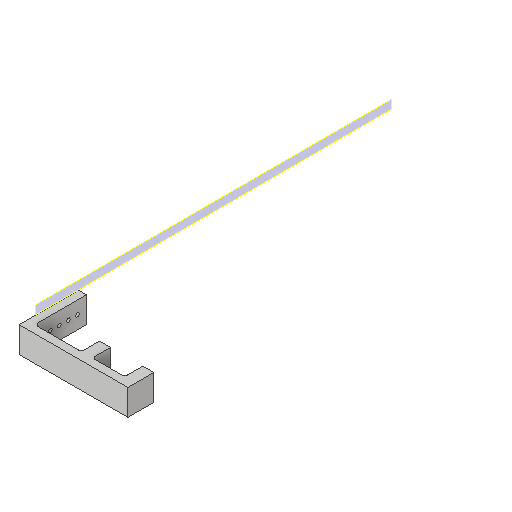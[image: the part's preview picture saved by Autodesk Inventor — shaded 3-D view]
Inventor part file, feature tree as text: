
AUTODESK INVENTOR PART (.ipt)
format: ipt  version: 2022 (Build 260153000, 153)  size: 144,384 bytes
history: native  units: mm
features: other x5, reference x4, extrude x3, sketch x3, plane x1, chamfer x1, projected_geometry x1
ambient origin geometry x8: Origin, YZ Plane, XZ Plane, XY Plane, X Axis, Y Axis, Z Axis, Center Point
bodies: Solid1 (feature_tree)
feature tree (18):
  plane  "Work Plane1"
  extrude  "Extrusion1"  Depth=20.0mm
  extrude  "Extrusion2"  Depth=5.0mm
  chamfer  "Chamfer1"  Distance=10.0mm
  extrude  "Extrusion3"  Depth=6.0mm TaperAngle=0.0deg
  sketch  "Sketch1"  dims[d0=40.0mm d1=20.0mm]
  reference  "Reference1"
  reference  "Reference2"
  sketch  "Sketch2"  dims[d2=2.8mm d3=5.0mm]
  projected_geometry  "Projected Loop1"
  sketch  "Sketch3"  dims[d4=10.0mm d5=60.0mm d7=7.0mm d8=10.0mm d10=10.0mm d12=6.0mm d13=0.0mm d14=84.0mm d15=6.0mm d16=8.5mm d17=36.0mm d18=8.5mm d19=10.0mm d20=0.0mm d21=2.0mm d22=2.0mm d23=45.0deg d24=10.0mm d25=0.0mm d26=4.9mm]
  reference  "Reference3"
  reference  "Reference4"
  other  "Assembly_neje_slide_y_wellplateholder_20mmrod.iam"
  other  "Assembly_neje_slide_y_20mmrod:1"
  other  "Neje_Base_Rod_20mm_250mm:1"
  other  "Neje_Rolls_small:1"
  other  "Neje_Rolls_small:2"
